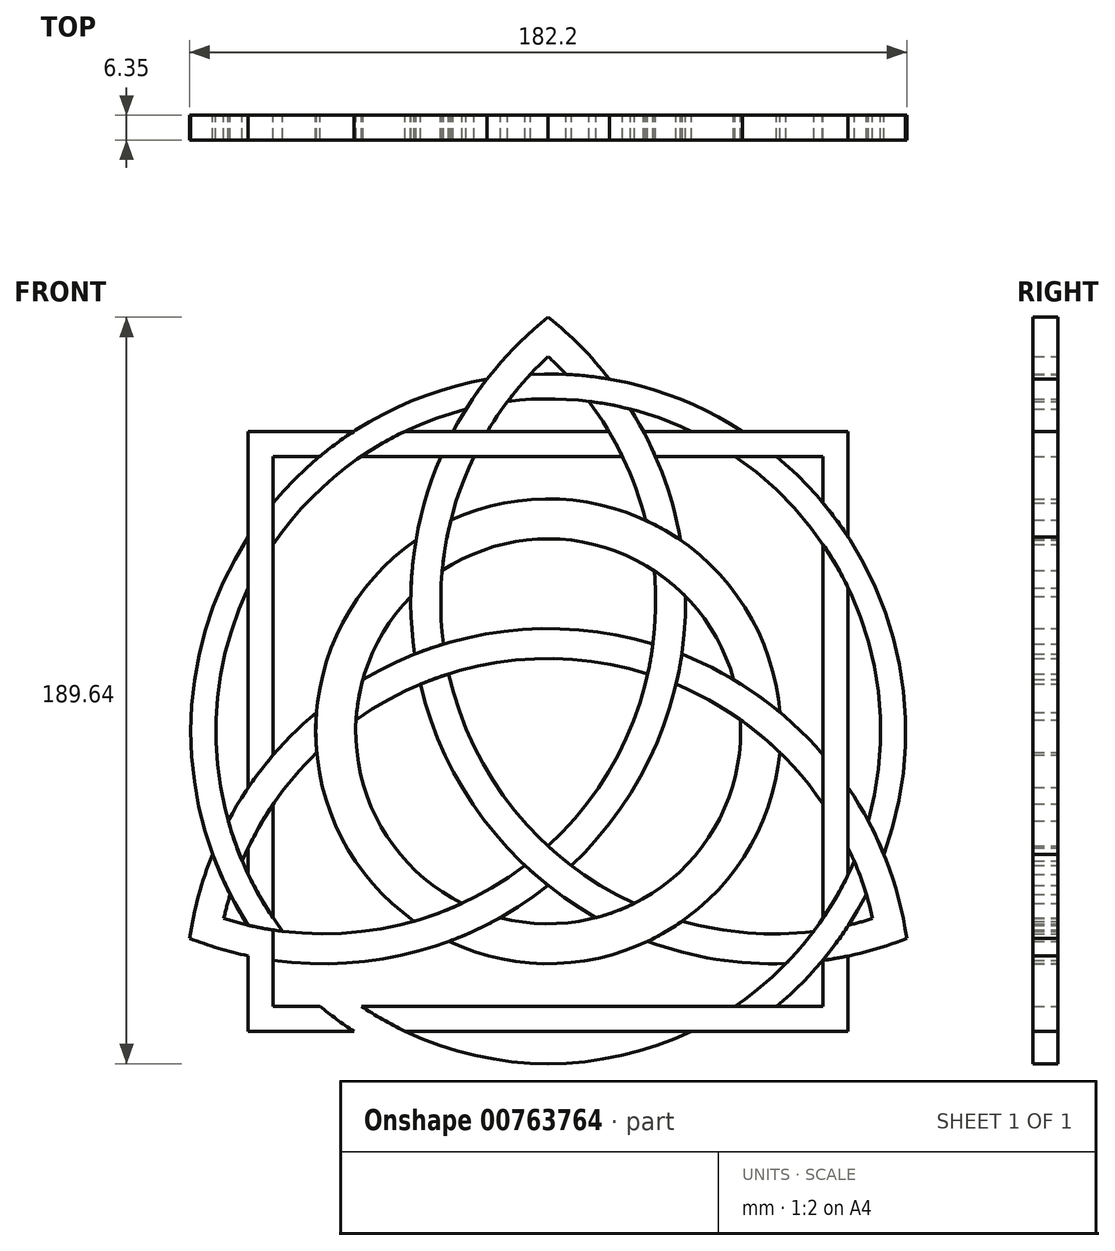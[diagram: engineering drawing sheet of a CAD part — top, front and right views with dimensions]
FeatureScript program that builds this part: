
annotation { "Feature Type Name" : "Feature", "Feature Type Description" : "" }
export const myFeature = defineFeature(function(context is Context, id is Id, definition is map)
    precondition{}
    {
        {
            var Q0;
            Q0=qCreatedBy(makeId("Front.planeOp"),FACE);
            var sketch = newSketch(context, id + "F0", { "sketchPlane" : qUnion([Q0])});
            skCircle(sketch, "E0", {"center": v(0, 0) * mm, "radius": 48.9 * mm});
            skCircle(sketch, "E1.0", {"center": v(0, 0) * mm, "radius": 59.06 * mm});
            skCircle(sketch, "E2.0", {"center": v(0, 0) * mm, "radius": 84.46 * mm});
            skCircle(sketch, "E3.0", {"center": v(0, 0) * mm, "radius": 90.8 * mm});
            skLineSegment(sketch, "E4.bottom", {"start": v(69.85, 69.85) * mm, "end": v(-69.85, 69.85) * mm});
            skLineSegment(sketch, "E4.top", {"start": v(69.85, -69.85) * mm, "end": v(-69.85, -69.85) * mm});
            skLineSegment(sketch, "E4.left", {"start": v(69.85, 69.85) * mm, "end": v(69.85, -69.85) * mm});
            skLineSegment(sketch, "E4.right", {"start": v(-69.85, 69.85) * mm, "end": v(-69.85, -69.85) * mm});
            skLineSegment(sketch, "E5.0", {"start": v(76.2, 76.2) * mm, "end": v(-76.2, 76.2) * mm});
            skLineSegment(sketch, "E5.1", {"start": v(76.2, 76.2) * mm, "end": v(76.2, -76.2) * mm});
            skLineSegment(sketch, "E5.2", {"start": v(76.2, -76.2) * mm, "end": v(-76.2, -76.2) * mm});
            skLineSegment(sketch, "E5.3", {"start": v(-76.2, 76.2) * mm, "end": v(-76.2, -76.2) * mm});
            skCircle(sketch, "E6.cCircle", {"center": v(0, 0) * mm, "radius": 66 * mm, "construction": true});
            skLineSegment(sketch, "E6.0", {"start": v(-114.3, 66) * mm, "end": v(114.3, 66) * mm, "construction": true});
            skLineSegment(sketch, "E6.1", {"start": v(114.3, 66) * mm, "end": v(0, -131.98) * mm, "construction": true});
            skLineSegment(sketch, "E6.2", {"start": v(0, -131.98) * mm, "end": v(-114.3, 66) * mm, "construction": true});
            skPoint(sketch, "E6.0.midPoint", {"position": v(0, 66) * mm});
            skLineSegment(sketch, "E7.0", {"start": v(-114.3, -66) * mm, "end": v(0, 131.98) * mm, "construction": true});
            skLineSegment(sketch, "E7.1", {"start": v(0, 131.98) * mm, "end": v(114.3, -66) * mm, "construction": true});
            skLineSegment(sketch, "E7.2", {"start": v(114.3, -66) * mm, "end": v(-114.3, -66) * mm, "construction": true});
            skPoint(sketch, "E7.0.midPoint", {"position": v(-57.15, 33) * mm});
            skLineSegment(sketch, "E8", {"start": v(0, 0) * mm, "end": v(0, 131.98) * mm, "construction": true});
            skLineSegment(sketch, "E9", {"start": v(0, 0) * mm, "end": v(114.3, -66) * mm, "construction": true});
            skLineSegment(sketch, "E10", {"start": v(0, 0) * mm, "end": v(-114.3, -66) * mm, "construction": true});
            skCircle(sketch, "E11", {"center": v(57.15, 33) * mm, "radius": 92.08 * mm});
            skCircle(sketch, "E12.0", {"center": v(57.15, 33) * mm, "radius": 84.45 * mm});
            skCircle(sketch, "E13", {"center": v(-57.15, 33) * mm, "radius": 92.08 * mm});
            skCircle(sketch, "E14", {"center": v(0, -66) * mm, "radius": 92.08 * mm});
            skCircle(sketch, "E15.0", {"center": v(-57.15, 33) * mm, "radius": 84.45 * mm});
            skCircle(sketch, "E16.0", {"center": v(0, -66) * mm, "radius": 84.45 * mm});
            skSolve(sketch);
        }
        {
            var Q0;
            Q0=qCreatedBy(makeId("Front.planeOp"),FACE);
            var sketch = newSketch(context, id + "F1", { "sketchPlane" : qUnion([Q0])});
            skArc(sketch, "E17.0", {"start": v(-91.1, -52.6) * mm, "mid": v(-83.74, -55.16) * mm, "end": v(-76.2, -57.09) * mm});
            skArc(sketch, "E18.0", {"start": v(-82.43, -47.59) * mm, "mid": v(-42.51, -50.18) * mm, "end": v(-5.88, -34.12) * mm});
            skArc(sketch, "E19.0", {"start": v(0, 105.19) * mm, "mid": v(-13.58, 91.94) * mm, "end": v(-24.16, 76.2) * mm});
            skArc(sketch, "E20.0", {"start": v(0, 95.18) * mm, "mid": v(-8.4, 86.25) * mm, "end": v(-15.42, 76.2) * mm});
            skArc(sketch, "E21.0", {"start": v(91.1, -52.6) * mm, "mid": v(85.81, -32.6) * mm, "end": v(76.2, -14.3) * mm});
            skArc(sketch, "E22.0", {"start": v(82.43, -47.59) * mm, "mid": v(79.82, -38.4) * mm, "end": v(76.2, -29.57) * mm});
            skArc(sketch, "E23.0", {"start": v(-15.58, 89.46) * mm, "mid": v(-45.52, 78.57) * mm, "end": v(-69.85, 58.02) * mm});
            skArc(sketch, "E24.0", {"start": v(-20.91, 81.83) * mm, "mid": v(-48.52, 69.12) * mm, "end": v(-69.85, 47.47) * mm});
            skArc(sketch, "E25.0", {"start": v(58.86, 4.81) * mm, "mid": v(29.77, 51) * mm, "end": v(-24.75, 53.62) * mm});
            skArc(sketch, "E26.0", {"start": v(47.1, 13.12) * mm, "mid": v(17.12, 45.8) * mm, "end": v(-26.94, 40.8) * mm});
            skLineSegment(sketch, "E27.0", {"start": v(76.2, 76.2) * mm, "end": v(24.16, 76.2) * mm});
            skLineSegment(sketch, "E28.0", {"start": v(69.85, 69.85) * mm, "end": v(27.23, 69.85) * mm});
            skLineSegment(sketch, "E29.0", {"start": v(-76.2, 76.2) * mm, "end": v(-76.2, -14.3) * mm});
            skLineSegment(sketch, "E30.0", {"start": v(-69.85, 69.85) * mm, "end": v(-69.85, -6) * mm});
            skLineSegment(sketch, "E31.0", {"start": v(76.2, -76.2) * mm, "end": v(-36.42, -76.2) * mm});
            skLineSegment(sketch, "E32.0", {"start": v(69.85, -69.85) * mm, "end": v(-47.47, -69.85) * mm});
            skLineSegment(sketch, "E33.0", {"start": v(69.85, 69.85) * mm, "end": v(69.85, 58.02) * mm});
            skLineSegment(sketch, "E34.0", {"start": v(76.2, 76.2) * mm, "end": v(76.2, 49.39) * mm});
            skArc(sketch, "E35.trimOffspring", {"start": v(4.52, 90.7) * mm, "mid": v(2.3, 92.98) * mm, "end": v(0, 95.18) * mm});
            skArc(sketch, "E36.trimOffspring", {"start": v(15.58, 89.46) * mm, "mid": v(8.26, 97.8) * mm, "end": v(0, 105.19) * mm});
            skArc(sketch, "E37.trimOffspring", {"start": v(36.42, 76.2) * mm, "mid": v(13.6, 83.35) * mm, "end": v(-10.3, 83.83) * mm});
            skArc(sketch, "E38.trimOffspring", {"start": v(49.39, 76.2) * mm, "mid": v(23.57, 87.7) * mm, "end": v(-4.52, 90.7) * mm});
            skLineSegment(sketch, "E39.trimOffspring", {"start": v(69.85, 47.47) * mm, "end": v(69.85, -47.47) * mm});
            skLineSegment(sketch, "E40.trimOffspring", {"start": v(76.2, 36.42) * mm, "end": v(76.2, -36.42) * mm});
            skArc(sketch, "E41.trimOffspring", {"start": v(85.26, -31.24) * mm, "mid": v(87.68, 23.63) * mm, "end": v(58.02, 69.85) * mm});
            skArc(sketch, "E42.trimOffspring", {"start": v(81.32, -22.8) * mm, "mid": v(79.33, 28.98) * mm, "end": v(47.47, 69.85) * mm});
            skLineSegment(sketch, "E43.trimOffspring", {"start": v(76.2, -49.28) * mm, "end": v(76.2, -49.39) * mm});
            skLineSegment(sketch, "E44.trimOffspring", {"start": v(69.85, -58.2) * mm, "end": v(69.85, -69.85) * mm});
            skArc(sketch, "E45.trimOffspring", {"start": v(76.28, -49.26) * mm, "mid": v(79.37, -48.48) * mm, "end": v(82.43, -47.59) * mm});
            skArc(sketch, "E46.trimOffspring", {"start": v(69.68, -58.22) * mm, "mid": v(80.56, -56.05) * mm, "end": v(91.1, -52.6) * mm});
            skLineSegment(sketch, "E47.trimOffspring", {"start": v(76.2, -57.09) * mm, "end": v(76.2, -76.2) * mm});
            skArc(sketch, "E48.trimOffspring", {"start": v(58.02, -69.85) * mm, "mid": v(70.85, -56.8) * mm, "end": v(80.8, -41.43) * mm});
            skArc(sketch, "E49.trimOffspring", {"start": v(47.47, -69.85) * mm, "mid": v(65.26, -53.6) * mm, "end": v(77.74, -33) * mm});
            skLineSegment(sketch, "E50.trimOffspring", {"start": v(-49.39, -76.2) * mm, "end": v(-76.2, -76.2) * mm});
            skLineSegment(sketch, "E51.trimOffspring", {"start": v(-58.02, -69.85) * mm, "end": v(-69.85, -69.85) * mm});
            skArc(sketch, "E52.trimOffspring", {"start": v(-60.4, -59.02) * mm, "mid": v(-14.75, -83.16) * mm, "end": v(36.42, -76.2) * mm});
            skArc(sketch, "E53.trimOffspring", {"start": v(-69.68, -58.22) * mm, "mid": v(-13.56, -89.79) * mm, "end": v(49.39, -76.2) * mm});
            skArc(sketch, "E54.trimOffspring", {"start": v(-69.85, -58.2) * mm, "mid": v(-32.98, -55.85) * mm, "end": v(0, -39.2) * mm});
            skArc(sketch, "E55.trimOffspring", {"start": v(-85.26, -31.24) * mm, "mid": v(-88.82, -41.74) * mm, "end": v(-91.1, -52.6) * mm});
            skArc(sketch, "E56.trimOffspring", {"start": v(-80.8, -41.43) * mm, "mid": v(-81.67, -44.5) * mm, "end": v(-82.43, -47.59) * mm});
            skLineSegment(sketch, "E57.trimOffspring", {"start": v(-76.2, -49.39) * mm, "end": v(-76.2, -76.2) * mm});
            skLineSegment(sketch, "E58.trimOffspring", {"start": v(-69.85, -50.5) * mm, "end": v(-69.85, -69.85) * mm});
            skLineSegment(sketch, "E59.trimOffspring", {"start": v(-76.2, -29.57) * mm, "end": v(-76.2, -36.42) * mm});
            skLineSegment(sketch, "E60.trimOffspring", {"start": v(-69.85, -18.52) * mm, "end": v(-69.85, -47.47) * mm});
            skArc(sketch, "E61.trimOffspring", {"start": v(-76.2, 49.39) * mm, "mid": v(-90.8, 0.07) * mm, "end": v(-76.28, -49.26) * mm});
            skArc(sketch, "E62.trimOffspring", {"start": v(-76.2, 36.42) * mm, "mid": v(-84.03, -8.43) * mm, "end": v(-67.45, -50.83) * mm});
            skArc(sketch, "E63.trimOffspring", {"start": v(-58.86, 4.81) * mm, "mid": v(-71.44, -7.9) * mm, "end": v(-81.32, -22.8) * mm});
            skArc(sketch, "E64.trimOffspring", {"start": v(-58.8, -5.38) * mm, "mid": v(-69.66, -18.24) * mm, "end": v(-77.74, -33) * mm});
            skArc(sketch, "E65.trimOffspring", {"start": v(-32.5, 11.96) * mm, "mid": v(-16.4, -22.4) * mm, "end": v(12.18, -47.35) * mm});
            skArc(sketch, "E66.trimOffspring", {"start": v(-25.28, 14.6) * mm, "mid": v(-8.54, -20.1) * mm, "end": v(21.86, -43.73) * mm});
            skArc(sketch, "E67.trimOffspring", {"start": v(26.6, 22.16) * mm, "mid": v(-11.2, 25.4) * mm, "end": v(-47.1, 13.12) * mm});
            skArc(sketch, "E68.trimOffspring", {"start": v(25.28, 14.6) * mm, "mid": v(-13.13, 17.44) * mm, "end": v(-48.8, 2.93) * mm});
            skArc(sketch, "E69.trimOffspring", {"start": v(69.85, -6) * mm, "mid": v(53.45, 8.98) * mm, "end": v(33.95, 19.6) * mm});
            skArc(sketch, "E70.trimOffspring", {"start": v(69.85, -18.52) * mm, "mid": v(53.4, -0.55) * mm, "end": v(32.5, 11.96) * mm});
            skArc(sketch, "E71.trimOffspring", {"start": v(-33.6, 48.57) * mm, "mid": v(-59.05, 0.28) * mm, "end": v(-34.06, -48.24) * mm});
            skArc(sketch, "E72.trimOffspring", {"start": v(-34.92, 34.23) * mm, "mid": v(-48.22, -8.07) * mm, "end": v(-21.86, -43.73) * mm});
            skArc(sketch, "E73.trimOffspring", {"start": v(24.75, 53.62) * mm, "mid": v(19.03, 69.45) * mm, "end": v(10.3, 83.83) * mm});
            skArc(sketch, "E74.trimOffspring", {"start": v(33.6, 48.57) * mm, "mid": v(28.88, 65.81) * mm, "end": v(20.91, 81.83) * mm});
            skArc(sketch, "E75.trimOffspring", {"start": v(34.06, -48.24) * mm, "mid": v(50.62, -51.2) * mm, "end": v(67.45, -50.83) * mm});
            skArc(sketch, "E76.trimOffspring", {"start": v(25.26, -53.38) * mm, "mid": v(42.56, -57.92) * mm, "end": v(60.4, -59.02) * mm});
            skArc(sketch, "E77.trimOffspring", {"start": v(-12.18, -47.35) * mm, "mid": v(31.1, -37.73) * mm, "end": v(48.8, 2.93) * mm});
            skArc(sketch, "E78.trimOffspring", {"start": v(-25.26, -53.38) * mm, "mid": v(29.28, -51.28) * mm, "end": v(58.8, -5.38) * mm});
            skArc(sketch, "E79.trimOffspring", {"start": v(5.88, -34.12) * mm, "mid": v(27.6, -3) * mm, "end": v(34.92, 34.23) * mm});
            skArc(sketch, "E80.trimOffspring", {"start": v(0, -29.19) * mm, "mid": v(21.67, 2.65) * mm, "end": v(26.94, 40.8) * mm});
            skLineSegment(sketch, "E81.trimOffspring", {"start": v(-58.02, 69.85) * mm, "end": v(-69.85, 69.85) * mm});
            skLineSegment(sketch, "E82.trimOffspring", {"start": v(-49.39, 76.2) * mm, "end": v(-76.2, 76.2) * mm});
            skArc(sketch, "E83.trimOffspring", {"start": v(-27.23, 69.85) * mm, "mid": v(-34.11, 45.2) * mm, "end": v(-33.95, 19.6) * mm});
            skArc(sketch, "E84.trimOffspring", {"start": v(-18.84, 69.85) * mm, "mid": v(-26.2, 46.57) * mm, "end": v(-26.6, 22.16) * mm});
            skLineSegment(sketch, "E85.trimOffspring", {"start": v(15.42, 76.2) * mm, "end": v(-36.42, 76.2) * mm});
            skLineSegment(sketch, "E86.trimOffspring", {"start": v(18.84, 69.85) * mm, "end": v(-47.47, 69.85) * mm});
            skSolve(sketch);
        }
        {
            var Q0;
            {var subQ1=sQuery(id+"F1.wireOp",EDGE,"E23.0");var subQ5=sQuery(id+"F1.wireOp",EDGE,"E19.0");var subQ6=makeQuery(id+"F1.imprint","INTERSECT",VERTEX,{"derivedFrom":[subQ5,subQ1]});Q0=makeQuery(id+"F1.imprint","IMPRINT",FACE,{"disambiguationData":[TD([[makeQuery(id+"F1.imprint","IMPRINT",EDGE,{"disambiguationData":[TD([[subQ6,-1.0]])],"derivedFrom":subQ5}),-1.0]])]});}
            var Q1;
            {var subQ0=sQuery(id+"F1.wireOp",EDGE,"E37.trimOffspring");var subQ7=sQuery(id+"F1.wireOp",EDGE,"E20.0");var subQ8=makeQuery(id+"F1.imprint","INTERSECT",VERTEX,{"derivedFrom":[subQ7,subQ0]});Q1=makeQuery(id+"F1.imprint","IMPRINT",FACE,{"disambiguationData":[TD([[makeQuery(id+"F1.imprint","IMPRINT",EDGE,{"disambiguationData":[TD([[subQ8,1.0]])],"derivedFrom":subQ7}),1.0]])]});}
            var Q2;
            {var subQ0=sQuery(id+"F1.wireOp",EDGE,"E41.trimOffspring");var subQ3=sQuery(id+"F1.wireOp",EDGE,"E21.0");var subQ4=makeQuery(id+"F1.imprint","INTERSECT",VERTEX,{"derivedFrom":[subQ3,subQ0]});Q2=makeQuery(id+"F1.imprint","IMPRINT",FACE,{"disambiguationData":[TD([[makeQuery(id+"F1.imprint","IMPRINT",EDGE,{"disambiguationData":[TD([[subQ4,-1.0]])],"derivedFrom":subQ3}),-1.0]])]});}
            var Q3;
            {var subQ3=sQuery(id+"F1.wireOp",EDGE,"E48.trimOffspring");var subQ4=sQuery(id+"F1.wireOp",EDGE,"E22.0");var subQ5=makeQuery(id+"F1.imprint","INTERSECT",VERTEX,{"derivedFrom":[subQ4,subQ3]});Q3=makeQuery(id+"F1.imprint","IMPRINT",FACE,{"disambiguationData":[TD([[makeQuery(id+"F1.imprint","IMPRINT",EDGE,{"disambiguationData":[TD([[subQ5,-1.0]])],"derivedFrom":subQ4}),1.0]])]});}
            var Q4;
            {var subQ0=sQuery(id+"F1.wireOp",EDGE,"E52.trimOffspring");var subQ1=sQuery(id+"F1.wireOp",EDGE,"E31.0");var subQ3=makeQuery(id+"F1.imprint","INTERSECT",VERTEX,{"disambiguationData":[OD(1.0)],"derivedFrom":[subQ1,subQ0]});Q4=makeQuery(id+"F1.imprint","IMPRINT",FACE,{"disambiguationData":[TD([[makeQuery(id+"F1.imprint","IMPRINT",EDGE,{"disambiguationData":[TD([[subQ3,1.0]])],"derivedFrom":subQ1}),1.0]])]});}
            var Q5;
            {var subQ10=sQuery(id+"F1.wireOp",EDGE,"E18.0");var subQ11=makeQuery(id+"F1.imprint","INTERSECT",VERTEX,{"derivedFrom":[subQ10,sQuery(id+"F1.wireOp",EDGE,"E58.trimOffspring")]});Q5=makeQuery(id+"F1.imprint","IMPRINT",FACE,{"disambiguationData":[TD([[makeQuery(id+"F1.imprint","IMPRINT",EDGE,{"disambiguationData":[TD([[subQ11,1.0]])],"derivedFrom":subQ10}),1.0]])]});}
            var Q6;
            {var subQ0=sQuery(id+"F1.wireOp",EDGE,"E71.trimOffspring");var subQ5=sQuery(id+"F1.wireOp",EDGE,"E18.0");var subQ6=makeQuery(id+"F1.imprint","INTERSECT",VERTEX,{"derivedFrom":[subQ5,subQ0]});Q6=makeQuery(id+"F1.imprint","IMPRINT",FACE,{"disambiguationData":[TD([[makeQuery(id+"F1.imprint","IMPRINT",EDGE,{"disambiguationData":[TD([[subQ6,-1.0]])],"derivedFrom":subQ5}),1.0]])]});}
            var Q7;
            {var subQ0=sQuery(id+"F1.wireOp",EDGE,"E69.trimOffspring");var subQ4=sQuery(id+"F1.wireOp",EDGE,"E25.0");var subQ5=makeQuery(id+"F1.imprint","INTERSECT",VERTEX,{"derivedFrom":[subQ4,subQ0]});Q7=makeQuery(id+"F1.imprint","IMPRINT",FACE,{"disambiguationData":[TD([[makeQuery(id+"F1.imprint","IMPRINT",EDGE,{"disambiguationData":[TD([[subQ5,-1.0]])],"derivedFrom":subQ4}),1.0]])]});}
            var Q8;
            {var subQ0=sQuery(id+"F1.wireOp",EDGE,"E77.trimOffspring");var subQ3=sQuery(id+"F1.wireOp",EDGE,"E54.trimOffspring");var subQ4=makeQuery(id+"F1.imprint","INTERSECT",VERTEX,{"derivedFrom":[subQ3,subQ0]});Q8=makeQuery(id+"F1.imprint","IMPRINT",FACE,{"disambiguationData":[TD([[makeQuery(id+"F1.imprint","IMPRINT",EDGE,{"disambiguationData":[TD([[subQ4,1.0]])],"derivedFrom":subQ3}),-1.0]])]});}
            extrude(context, id + "F2", {"entities" : qUnion([Q0, Q1, Q2, Q3, Q4, Q5, Q6, Q7, Q8]), "depth" : 6.35 * mm, "offsetDistance" : 25.4 * mm});
        }
        {
            var Q0;
            {var subQ0=sQuery(id+"F1.wireOp",EDGE,"E35.trimOffspring");Q0=makeQuery(id+"F1.imprint","IMPRINT",FACE,{"disambiguationData":[TD([[makeQuery(id+"F1.imprint","IMPRINT",EDGE,{"derivedFrom":subQ0}),-1.0]])]});}
            var Q1;
            {var subQ0=sQuery(id+"F1.wireOp",EDGE,"E73.trimOffspring");var subQ3=sQuery(id+"F1.wireOp",EDGE,"E25.0");var subQ4=makeQuery(id+"F1.imprint","INTERSECT",VERTEX,{"derivedFrom":[subQ3,subQ0]});Q1=makeQuery(id+"F1.imprint","IMPRINT",FACE,{"disambiguationData":[TD([[makeQuery(id+"F1.imprint","IMPRINT",EDGE,{"disambiguationData":[TD([[subQ4,1.0]])],"derivedFrom":subQ3}),-1.0]])]});}
            var Q2;
            {var subQ0=sQuery(id+"F1.wireOp",EDGE,"E79.trimOffspring");var subQ7=sQuery(id+"F1.wireOp",EDGE,"E26.0");var subQ8=makeQuery(id+"F1.imprint","INTERSECT",VERTEX,{"derivedFrom":[subQ7,subQ0]});Q2=makeQuery(id+"F1.imprint","IMPRINT",FACE,{"disambiguationData":[TD([[makeQuery(id+"F1.imprint","IMPRINT",EDGE,{"disambiguationData":[TD([[subQ8,-1.0]])],"derivedFrom":subQ7}),1.0]])]});}
            var Q3;
            {var subQ0=sQuery(id+"F1.wireOp",EDGE,"E58.trimOffspring");var subQ3=sQuery(id+"F1.wireOp",EDGE,"E18.0");var subQ4=makeQuery(id+"F1.imprint","INTERSECT",VERTEX,{"derivedFrom":[subQ3,subQ0]});Q3=makeQuery(id+"F1.imprint","IMPRINT",FACE,{"disambiguationData":[TD([[makeQuery(id+"F1.imprint","IMPRINT",EDGE,{"disambiguationData":[TD([[subQ4,-1.0]])],"derivedFrom":subQ3}),-1.0]])]});}
            var Q4;
            {var subQ5=sQuery(id+"F1.wireOp",EDGE,"E17.0");Q4=makeQuery(id+"F1.imprint","IMPRINT",FACE,{"disambiguationData":[TD([[makeQuery(id+"F1.imprint","IMPRINT",EDGE,{"derivedFrom":subQ5}),1.0]])]});}
            var Q5;
            {var subQ0=sQuery(id+"F1.wireOp",EDGE,"E63.trimOffspring");var subQ2=sQuery(id+"F1.wireOp",EDGE,"E62.trimOffspring");var subQ3=makeQuery(id+"F1.imprint","INTERSECT",VERTEX,{"derivedFrom":[subQ2,subQ0]});Q5=makeQuery(id+"F1.imprint","IMPRINT",FACE,{"disambiguationData":[TD([[makeQuery(id+"F1.imprint","IMPRINT",EDGE,{"disambiguationData":[TD([[subQ3,-1.0]])],"derivedFrom":subQ2}),1.0]])]});}
            var Q6;
            {var subQ0=sQuery(id+"F1.wireOp",EDGE,"E46.trimOffspring");var subQ9=sQuery(id+"F1.wireOp",EDGE,"E21.0");var subQ15=makeQuery(id+"F1.imprint","INTERSECT",VERTEX,{"derivedFrom":[subQ9,subQ0]});Q6=makeQuery(id+"F1.imprint","IMPRINT",FACE,{"disambiguationData":[TD([[makeQuery(id+"F1.imprint","IMPRINT",EDGE,{"disambiguationData":[TD([[subQ15,-1.0]])],"derivedFrom":subQ9}),1.0]])]});}
            var Q7;
            {var subQ0=sQuery(id+"F1.wireOp",EDGE,"E75.trimOffspring");Q7=makeQuery(id+"F1.imprint","IMPRINT",FACE,{"disambiguationData":[TD([[makeQuery(id+"F1.imprint","IMPRINT",EDGE,{"derivedFrom":subQ0}),-1.0]])]});}
            extrude(context, id + "F3", {"entities" : qUnion([Q0, Q1, Q2, Q3, Q4, Q5, Q6, Q7]), "depth" : 6.35 * mm, "offsetDistance" : 25.4 * mm});
        }
        {
            var Q0;
            {var subQ0=sQuery(id+"F1.wireOp",EDGE,"E83.trimOffspring");var subQ2=sQuery(id+"F1.wireOp",EDGE,"E67.trimOffspring");var subQ3=makeQuery(id+"F1.imprint","INTERSECT",VERTEX,{"derivedFrom":[subQ2,subQ0]});Q0=makeQuery(id+"F1.imprint","IMPRINT",FACE,{"disambiguationData":[TD([[makeQuery(id+"F1.imprint","IMPRINT",EDGE,{"disambiguationData":[TD([[subQ3,1.0]])],"derivedFrom":subQ2}),-1.0]])]});}
            var Q1;
            {var subQ4=sQuery(id+"F1.wireOp",EDGE,"E65.trimOffspring");var subQ8=makeQuery(id+"F1.imprint","INTERSECT",VERTEX,{"derivedFrom":[sQuery(id+"F1.wireOp",EDGE,"E18.0"),subQ4]});Q1=makeQuery(id+"F1.imprint","IMPRINT",FACE,{"disambiguationData":[TD([[makeQuery(id+"F1.imprint","IMPRINT",EDGE,{"disambiguationData":[TD([[subQ8,1.0]])],"derivedFrom":subQ4}),1.0]])]});}
            var Q2;
            {var subQ0=sQuery(id+"F1.wireOp",EDGE,"E69.trimOffspring");var subQ5=sQuery(id+"F1.wireOp",EDGE,"E39.trimOffspring");var subQ6=makeQuery(id+"F1.imprint","INTERSECT",VERTEX,{"derivedFrom":[subQ5,subQ0]});Q2=makeQuery(id+"F1.imprint","IMPRINT",FACE,{"disambiguationData":[TD([[makeQuery(id+"F1.imprint","IMPRINT",EDGE,{"disambiguationData":[TD([[subQ6,-1.0]])],"derivedFrom":subQ5}),-1.0]])]});}
            extrude(context, id + "F4", {"entities" : qUnion([Q0, Q1, Q2]), "depth" : 6.35 * mm, "offsetDistance" : 25.4 * mm});
        }
        {
            var Q0;
            {var subQ2=sQuery(id+"F1.wireOp",EDGE,"E80.trimOffspring");var subQ4=sQuery(id+"F1.wireOp",EDGE,"E67.trimOffspring");var subQ5=makeQuery(id+"F1.imprint","INTERSECT",VERTEX,{"derivedFrom":[subQ4,subQ2]});Q0=makeQuery(id+"F1.imprint","IMPRINT",FACE,{"disambiguationData":[TD([[makeQuery(id+"F1.imprint","IMPRINT",EDGE,{"disambiguationData":[TD([[subQ5,-1.0]])],"derivedFrom":subQ4}),1.0]])]});}
            var Q1;
            {var subQ2=sQuery(id+"F1.wireOp",EDGE,"E42.trimOffspring");var subQ5=sQuery(id+"F1.wireOp",EDGE,"E39.trimOffspring");var subQ9=makeQuery(id+"F1.imprint","INTERSECT",VERTEX,{"derivedFrom":[subQ5,subQ2]});Q1=makeQuery(id+"F1.imprint","IMPRINT",FACE,{"disambiguationData":[TD([[makeQuery(id+"F1.imprint","IMPRINT",EDGE,{"disambiguationData":[TD([[subQ9,-1.0]])],"derivedFrom":subQ5}),1.0]])]});}
            var Q2;
            {var subQ0=sQuery(id+"F1.wireOp",EDGE,"E33.0");Q2=makeQuery(id+"F1.imprint","IMPRINT",FACE,{"disambiguationData":[TD([[makeQuery(id+"F1.imprint","IMPRINT",EDGE,{"derivedFrom":subQ0}),1.0]])]});}
            var Q3;
            {var subQ0=sQuery(id+"F1.wireOp",EDGE,"E85.trimOffspring");var subQ4=sQuery(id+"F1.wireOp",EDGE,"E24.0");var subQ5=makeQuery(id+"F1.imprint","INTERSECT",VERTEX,{"derivedFrom":[subQ4,subQ0]});Q3=makeQuery(id+"F1.imprint","IMPRINT",FACE,{"disambiguationData":[TD([[makeQuery(id+"F1.imprint","IMPRINT",EDGE,{"disambiguationData":[TD([[subQ5,-1.0]])],"derivedFrom":subQ4}),1.0]])]});}
            var Q4;
            {var subQ6=sQuery(id+"F1.wireOp",EDGE,"E81.trimOffspring");Q4=makeQuery(id+"F1.imprint","IMPRINT",FACE,{"disambiguationData":[TD([[makeQuery(id+"F1.imprint","IMPRINT",EDGE,{"derivedFrom":subQ6}),-1.0]])]});}
            var Q5;
            {var subQ0=sQuery(id+"F1.wireOp",EDGE,"E59.trimOffspring");Q5=makeQuery(id+"F1.imprint","IMPRINT",FACE,{"disambiguationData":[TD([[makeQuery(id+"F1.imprint","IMPRINT",EDGE,{"derivedFrom":subQ0}),1.0]])]});}
            var Q6;
            {var subQ5=sQuery(id+"F1.wireOp",EDGE,"E50.trimOffspring");Q6=makeQuery(id+"F1.imprint","IMPRINT",FACE,{"disambiguationData":[TD([[makeQuery(id+"F1.imprint","IMPRINT",EDGE,{"derivedFrom":subQ5}),-1.0]])]});}
            var Q7;
            {var subQ0=sQuery(id+"F1.wireOp",EDGE,"E44.trimOffspring");Q7=makeQuery(id+"F1.imprint","IMPRINT",FACE,{"disambiguationData":[TD([[makeQuery(id+"F1.imprint","IMPRINT",EDGE,{"derivedFrom":subQ0}),1.0]])]});}
            var Q8;
            {var subQ0=sQuery(id+"F1.wireOp",EDGE,"E43.trimOffspring");Q8=makeQuery(id+"F1.imprint","IMPRINT",FACE,{"disambiguationData":[TD([[makeQuery(id+"F1.imprint","IMPRINT",EDGE,{"derivedFrom":subQ0}),-1.0]])]});}
            var Q9;
            {var subQ0=sQuery(id+"F1.wireOp",EDGE,"E61.trimOffspring");var subQ1=sQuery(id+"F1.wireOp",EDGE,"E18.0");var subQ2=makeQuery(id+"F1.imprint","INTERSECT",VERTEX,{"derivedFrom":[subQ1,subQ0]});Q9=makeQuery(id+"F1.imprint","IMPRINT",FACE,{"disambiguationData":[TD([[makeQuery(id+"F1.imprint","IMPRINT",EDGE,{"disambiguationData":[TD([[subQ2,1.0]])],"derivedFrom":subQ1}),1.0]])]});}
            extrude(context, id + "F5", {"entities" : qUnion([Q0, Q1, Q2, Q3, Q4, Q5, Q6, Q7, Q8, Q9]), "depth" : 6.35 * mm, "offsetDistance" : 25.4 * mm});
        }
    });
